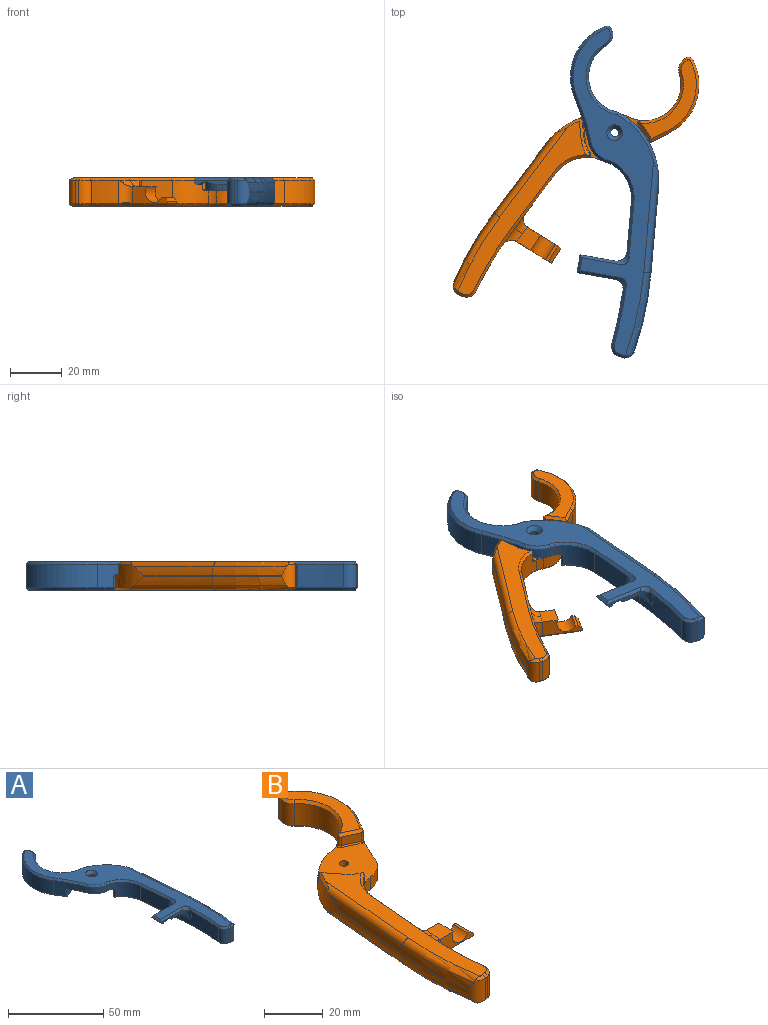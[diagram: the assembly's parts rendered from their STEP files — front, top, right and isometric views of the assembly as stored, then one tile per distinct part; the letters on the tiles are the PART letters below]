
ASSEMBLY  parts=2 mates=1
PART A: 92 faces, bbox 47.6x127.5x23.3 mm
  f0: plane 80.94x16.23mm, normal (0,0,-1), area 509mm2, adj f31,f32,f33,f34,f35,f36,f37,f38
  f1: cylinder r=30mm len=25.84mm, axis (0,0,-1), area 192mm2, adj f2,f11,f14,f31,f47,f66,f68,f69
  f2: cylinder r=14mm len=24.68mm, axis (0,0,-1), area 274.9mm2, adj f1,f14,f18,f45,f57,f81,f89
  f3: plane 9x0.51mm, normal (0.91,0.42,0), area 5.1mm2, adj f18,f26,f41,f60
  f4: cylinder r=21mm len=29.26mm, axis (0,0,-1), area 301.5mm2, adj f19,f26,f42,f63
  f5: cylinder r=10mm len=8.33mm, axis (0,0,-1), area 43.8mm2, adj f14,f19,f46,f91
  f6: plane 26.84x9mm, normal (-1,-0.09,0), area 200.4mm2, adj f7,f27,f37,f49,f75,f77
  f7: cylinder r=150mm len=28.8mm, axis (0,0,-1), area 214.7mm2, adj f6,f29,f39,f56,f76,f78
  f8: plane 9x1.29mm, normal (-0.18,-0.98,0), area 11.8mm2, adj f29,f30,f36,f53
  f9: cylinder r=130mm len=30.93mm, axis (0,0,-1), area 7.1mm2, adj f11,f30,f65,f67
  f10: cylinder r=1.57mm len=3.5mm, axis (0,0,-1), area 34.6mm2, adj f14,f64
  f11: plane 33.28x2.91mm, normal (1,0.09,0), area 7.7mm2, adj f1,f9,f66,f68
  f12: plane 125.47x42.7mm, normal (0,0,1), area 1111.8mm2, adj f40,f41,f42,f43,f44,f45,f46,f47
  f13: plane 33.8x13.25mm, normal (0,0,-1), area 182.3mm2, adj f57,f58,f59,f60,f61,f62,f63
  f14: plane 27.98x22.36mm, normal (0,0,-1), area 362.7mm2, adj f1,f2,f5,f10,f19,f27,f83,f84
  f15: plane 6.71x4.5mm, normal (0.42,-0.91,0), area 33.3mm2, adj f59,f80,f81,f88
  f16: cylinder r=11mm len=4.5mm, axis (0,0,1), area 24.9mm2, adj f17,f33,f79,f85
  f17: plane 5.87x4.59mm, normal (-0.79,0.62,0), area 33.5mm2, adj f16,f32,f82,f84
  f18: cylinder r=5mm len=9mm, axis (0,0,-1), area 58.7mm2, adj f2,f3,f43,f58
  f19: cylinder r=100mm len=16.45mm, axis (0,0,1), area 107.6mm2, adj f4,f5,f14,f44,f61,f80,f87
  f20: plane 14.83x1.7mm, normal (0,-1,0), area 19.4mm2, adj f21,f22,f23,f24,f28,f54,f76,f78
  f21: plane 7x0.2mm, normal (-1,0,0), area 1.4mm2, adj f20,f25,f28,f52
  f22: plane 7x0.64mm, normal (0,0,-1), area 4.5mm2, adj f20,f23,f25,f28
  f23: cylinder r=4mm len=7mm, axis (0,-1,0), area 44.5mm2, adj f20,f22,f24,f25
  f24: plane 7.02x6.78mm, normal (0,0,-1), area 45.6mm2, adj f20,f23,f25,f75,f77,f78
  f25: plane 13.72x1.7mm, normal (0,1,0), area 17.5mm2, adj f21,f22,f23,f24,f28,f50,f75
  f26: cylinder r=2mm len=9mm, axis (0,0,-1), area 30.2mm2, adj f3,f4,f40,f62
  f27: cylinder r=15mm len=12.38mm, axis (0,0,-1), area 132.3mm2, adj f6,f14,f35,f48,f79,f86,f91
  f28: plane 7x1.5mm, normal (-0.71,0,-0.71), area 14.8mm2, adj f20,f21,f22,f25
  f29: cylinder r=4mm len=9mm, axis (0,0,-1), area 53.7mm2, adj f7,f8,f38,f55
  f30: cylinder r=4mm len=9mm, axis (0,0,-1), area 47.1mm2, adj f8,f9,f34,f51,f65,f67,f70,f72
  f31: cone r=29mm half-angle=45deg, axis (0,0,1), area 12.5mm2, adj f0,f1,f32,f71,f82
  f32: plane 7.06x5.58mm, normal (-0.56,0.44,-0.71), area 11.2mm2, adj f0,f17,f31,f33,f82
  f33: cone r=12mm half-angle=45deg, axis (0,0,-1), area 8.8mm2, adj f0,f16,f32,f35,f79
  f34: cone r=3mm half-angle=45deg, axis (0,0,1), area 4.2mm2, adj f0,f30,f36,f72
  f35: cone r=16mm half-angle=45deg, axis (0,0,-1), area 20.6mm2, adj f0,f27,f33,f37,f79
  f36: plane 1.48x1.22mm, normal (-0.13,-0.7,-0.71), area 1.9mm2, adj f0,f8,f34,f38
  f37: plane 26.92x3.34mm, normal (-0.7,-0.06,-0.71), area 38.1mm2, adj f0,f6,f35,f39
  f38: cone r=3mm half-angle=45deg, axis (0,0,1), area 7.4mm2, adj f0,f29,f36,f39
  f39: cone r=150mm half-angle=45deg, axis (0,0,-1), area 40.9mm2, adj f0,f7,f37,f38
  f40: cone r=1mm half-angle=45deg, axis (0,0,-1), area 3.6mm2, adj f12,f26,f41,f42
  f41: plane 1.14x1mm, normal (0.64,0.3,0.71), area 0.8mm2, adj f3,f12,f40,f43
  f42: cone r=21mm half-angle=45deg, axis (0,0,-1), area 46.3mm2, adj f4,f12,f40,f44
  f43: cone r=4mm half-angle=45deg, axis (0,0,-1), area 8.3mm2, adj f12,f18,f41,f45
  f44: cone r=101mm half-angle=45deg, axis (0,0,1), area 26.3mm2, adj f12,f19,f42,f46
  f45: cone r=15mm half-angle=45deg, axis (0,0,1), area 49.9mm2, adj f2,f12,f43,f47
  f46: cone r=10mm half-angle=45deg, axis (0,0,-1), area 15.1mm2, adj f5,f12,f44,f90,f91
  f47: cone r=30mm half-angle=45deg, axis (0,0,-1), area 37.8mm2, adj f1,f12,f45,f69
  f48: cone r=16mm half-angle=45deg, axis (0,0,1), area 25mm2, adj f12,f27,f49,f90,f91
  f49: plane 21.93x2.99mm, normal (-0.7,-0.06,0.71), area 30.3mm2, adj f6,f12,f48,f73,f75
  f50: plane 16.17x1.23mm, normal (0,0.71,0.71), area 21.4mm2, adj f12,f25,f52,f73,f75
  f51: cone r=3mm half-angle=45deg, axis (0,0,-1), area 4.2mm2, adj f12,f30,f53,f70
  f52: plane 7x1mm, normal (-0.71,0,0.71), area 8.5mm2, adj f12,f21,f50,f54
  f53: plane 1.48x1.22mm, normal (-0.13,-0.7,0.71), area 1.9mm2, adj f8,f12,f51,f55
  f54: plane 16.97x1.19mm, normal (0,-0.71,0.71), area 22.6mm2, adj f12,f20,f52,f74,f76
  f55: cone r=3mm half-angle=45deg, axis (0,0,-1), area 7.4mm2, adj f12,f29,f53,f56
  f56: cone r=151mm half-angle=45deg, axis (0,0,1), area 32.2mm2, adj f7,f12,f55,f74,f76
  f57: cone r=14mm half-angle=45deg, axis (0,0,-1), area 41.1mm2, adj f2,f13,f58,f59,f81
  f58: cone r=4mm half-angle=45deg, axis (0,0,1), area 8.3mm2, adj f13,f18,f57,f60
  f59: plane 8.29x4.39mm, normal (0.3,-0.64,-0.71), area 11.8mm2, adj f13,f15,f57,f61,f80,f81
  f60: plane 1.14x1mm, normal (0.64,0.3,-0.71), area 0.8mm2, adj f3,f13,f58,f62
  f61: cone r=101mm half-angle=45deg, axis (0,0,-1), area 9.9mm2, adj f13,f19,f59,f63,f80
  f62: cone r=1mm half-angle=45deg, axis (0,0,1), area 3.6mm2, adj f13,f26,f60,f63
  f63: cone r=20mm half-angle=45deg, axis (0,0,1), area 46.3mm2, adj f4,f13,f61,f62
  f64: cone r=1.57mm half-angle=45deg, axis (0,0,1), area 31mm2, adj f10,f12
  f65: torus R=115mm, axis (0,0,-1), area 111.4mm2, adj f9,f30,f66,f72
  f66: cylinder r=15mm len=38.21mm, axis (0.09,-1,0), area 125.3mm2, adj f1,f11,f65,f71
  f67: torus R=115mm, axis (0,0,1), area 111.4mm2, adj f9,f30,f68,f70
  f68: cylinder r=15mm len=38.21mm, axis (-0.09,1,0), area 125.3mm2, adj f1,f11,f67,f69
  f69: cylinder r=2.5mm len=43.62mm, axis (-0.09,1,0), area 137.8mm2, adj f1,f12,f47,f68,f70
  f70: torus R=127.16mm, axis (0,0,1), area 110.5mm2, adj f12,f30,f51,f67,f69
  f71: cylinder r=2.5mm len=43.62mm, axis (0.09,-1,0), area 137.8mm2, adj f0,f1,f31,f66,f72
  f72: torus R=127.16mm, axis (0,0,1), area 110.5mm2, adj f0,f30,f34,f65,f71
  f73: cylinder r=4mm len=4.23mm, axis (-0.61,0.56,-0.56), area 9.1mm2, adj f12,f49,f50,f75
  f74: bspline ~16.93x16.54mm, area 7.9mm2, adj f12,f54,f56,f76
  f75: cylinder r=4mm len=5.7mm, axis (0,0,1), area 18.6mm2, adj f6,f24,f25,f49,f50,f73,f77
  f76: cylinder r=4mm len=5.7mm, axis (0,0,-1), area 19mm2, adj f7,f20,f54,f56,f74,f78
  f77: cylinder r=4mm len=7.7mm, axis (-0.09,1,0), area 33.8mm2, adj f6,f24,f75,f78
  f78: torus R=146mm, axis (0,0,-1), area 32.9mm2, adj f7,f20,f24,f76,f77
  f79: cylinder r=1mm len=5.06mm, axis (0,0,1), area 10.3mm2, adj f16,f27,f33,f35,f86
  f80: cylinder r=1mm len=4.77mm, axis (0,0,1), area 7mm2, adj f15,f19,f59,f61,f87
  f81: cylinder r=1mm len=5.08mm, axis (0,0,-1), area 10.7mm2, adj f2,f15,f57,f59,f89
  f82: cylinder r=1mm len=4.89mm, axis (0,0,-1), area 8.7mm2, adj f1,f17,f31,f32,f83
  f83: torus R=1.5mm, axis (0,0,1), area 1.3mm2, adj f1,f14,f82,f84
  f84: cylinder r=0.5mm len=6.18mm, axis (-0.62,-0.79,0), area 5.9mm2, adj f14,f17,f83,f85
  f85: torus R=10.5mm, axis (0,0,1), area 4.3mm2, adj f14,f16,f84,f86
  f86: torus R=1.5mm, axis (0,0,1), area 1.6mm2, adj f14,f27,f79,f85
  f87: torus R=1.5mm, axis (0,0,1), area 1mm2, adj f14,f19,f80,f88
  f88: cylinder r=0.5mm len=6.92mm, axis (0.91,0.42,0), area 5.8mm2, adj f14,f15,f87,f89
  f89: torus R=1.5mm, axis (0,0,1), area 1.7mm2, adj f2,f14,f81,f88
  f90: bspline ~2.78x2.43mm, area 2.8mm2, adj f12,f46,f48,f91
  f91: cylinder r=10mm len=4mm, axis (0,0,-1), area 13mm2, adj f5,f14,f27,f46,f48,f90
PART B: 91 faces, bbox 47.6x127.5x23.3 mm
  f0: cylinder r=150mm len=20.94mm, axis (0,0,-1), area 188.7mm2, adj f30,f39,f56,f73
  f1: plane 20.03x9mm, normal (1,-0.09,0), area 181mm2, adj f27,f37,f49,f77
  f2: cylinder r=30mm len=25.84mm, axis (0,0,-1), area 210.7mm2, adj f6,f8,f17,f31,f47,f65,f67,f68
  f3: cylinder r=10mm len=8.33mm, axis (0,0,-1), area 54.7mm2, adj f17,f19,f46,f89
  f4: cylinder r=21mm len=29.26mm, axis (0,0,-1), area 301.5mm2, adj f19,f26,f42,f63
  f5: cylinder r=1.57mm len=6mm, axis (0,0,-1), area 59.4mm2, adj f13,f17
  f6: cylinder r=14mm len=24.68mm, axis (0,0,-1), area 281.4mm2, adj f2,f17,f18,f45,f57,f80,f86
  f7: plane 33.8x13.25mm, normal (0,0,1), area 182.3mm2, adj f57,f58,f59,f60,f61,f62,f63
  f8: plane 33.28x2.91mm, normal (-1,0.09,0), area 7.7mm2, adj f2,f9,f65,f67
  f9: cylinder r=130mm len=30.93mm, axis (0,0,-1), area 7.1mm2, adj f8,f29,f64,f66
  f10: plane 9x1.29mm, normal (0.18,-0.98,0), area 11.8mm2, adj f29,f30,f36,f53
  f11: plane 9x0.51mm, normal (-0.91,0.42,0), area 5.1mm2, adj f18,f26,f41,f60
  f12: plane 80.94x16.23mm, normal (0,0,1), area 509mm2, adj f31,f32,f33,f34,f35,f36,f37,f38
  f13: plane 125.47x42.7mm, normal (0,0,-1), area 1138.7mm2, adj f5,f40,f41,f42,f43,f44,f45,f46
  f14: plane 6.71x3.5mm, normal (-0.42,-0.91,0), area 25.9mm2, adj f59,f79,f80,f87
  f15: plane 5.87x4.59mm, normal (0.79,0.62,0), area 26.1mm2, adj f16,f32,f81,f84
  f16: cylinder r=11mm len=4.33mm, axis (0,0,1), area 19.3mm2, adj f15,f33,f78,f83
  f17: plane 27.98x22.36mm, normal (0,0,1), area 362.7mm2, adj f2,f3,f5,f6,f19,f27,f82,f83
  f18: cylinder r=5mm len=9mm, axis (0,0,-1), area 58.7mm2, adj f6,f11,f43,f58
  f19: cylinder r=100mm len=16.45mm, axis (0,0,1), area 119.5mm2, adj f3,f4,f17,f44,f61,f79,f88
  f20: plane 15.26x6.5mm, normal (0,1,0), area 49mm2, adj f21,f22,f23,f24,f28,f50,f77
  f21: plane 7x6.46mm, normal (0,0,1), area 43.4mm2, adj f20,f24,f25,f73,f74,f75,f77
  f22: plane 7x1mm, normal (1,0,0), area 7mm2, adj f20,f25,f28,f52
  f23: plane 7x1.04mm, normal (0,0,1), area 7.3mm2, adj f20,f24,f25,f28
  f24: cylinder r=4mm len=7.46mm, axis (0,-1,0), area 88mm2, adj f20,f21,f23,f25
  f25: plane 15.83x6.5mm, normal (0,-1,0), area 52.6mm2, adj f21,f22,f23,f24,f28,f54,f73
  f26: cylinder r=2mm len=9mm, axis (0,0,-1), area 30.2mm2, adj f4,f11,f40,f62
  f27: cylinder r=15mm len=12.38mm, axis (0,0,-1), area 134.5mm2, adj f1,f17,f35,f48,f78,f82,f89
  f28: plane 7x1.5mm, normal (0.71,0,0.71), area 14.8mm2, adj f20,f22,f23,f25
  f29: cylinder r=4mm len=9mm, axis (0,0,-1), area 47.1mm2, adj f9,f10,f34,f51,f64,f66,f69,f71
  f30: cylinder r=4mm len=9mm, axis (0,0,-1), area 53.7mm2, adj f0,f10,f38,f55
  f31: cone r=29mm half-angle=45deg, axis (0,0,-1), area 12.5mm2, adj f2,f12,f32,f70,f81
  f32: plane 7.06x5.58mm, normal (0.56,0.44,0.71), area 11.2mm2, adj f12,f15,f31,f33,f81
  f33: cone r=11mm half-angle=45deg, axis (0,0,1), area 8.8mm2, adj f12,f16,f32,f35,f78
  f34: cone r=3mm half-angle=45deg, axis (0,0,-1), area 4.2mm2, adj f12,f29,f36,f71
  f35: cone r=16mm half-angle=45deg, axis (0,0,1), area 20.6mm2, adj f12,f27,f33,f37,f78
  f36: plane 1.48x1.22mm, normal (0.13,-0.7,0.71), area 1.9mm2, adj f10,f12,f34,f38
  f37: plane 26.92x3.34mm, normal (0.7,-0.06,0.71), area 38.1mm2, adj f1,f12,f35,f39,f74
  f38: cone r=3mm half-angle=45deg, axis (0,0,-1), area 7.4mm2, adj f12,f30,f36,f39
  f39: cone r=150mm half-angle=45deg, axis (0,0,1), area 40.9mm2, adj f0,f12,f37,f38,f75
  f40: cone r=1mm half-angle=45deg, axis (0,0,1), area 3.6mm2, adj f13,f26,f41,f42
  f41: plane 1.14x1mm, normal (-0.64,0.3,-0.71), area 0.8mm2, adj f11,f13,f40,f43
  f42: cone r=21mm half-angle=45deg, axis (0,0,1), area 46.3mm2, adj f4,f13,f40,f44
  f43: cone r=4mm half-angle=45deg, axis (0,0,1), area 8.3mm2, adj f13,f18,f41,f45
  f44: cone r=101mm half-angle=45deg, axis (0,0,-1), area 26.3mm2, adj f13,f19,f42,f46
  f45: cone r=15mm half-angle=45deg, axis (0,0,-1), area 49.9mm2, adj f6,f13,f43,f47
  f46: cone r=10mm half-angle=45deg, axis (0,0,1), area 15.1mm2, adj f3,f13,f44,f89,f90
  f47: cone r=30mm half-angle=45deg, axis (0,0,1), area 37.8mm2, adj f2,f13,f45,f68
  f48: cone r=16mm half-angle=45deg, axis (0,0,-1), area 25mm2, adj f13,f27,f49,f89,f90
  f49: plane 21.88x2.94mm, normal (0.7,-0.06,-0.71), area 30.3mm2, adj f1,f13,f48,f76,f77
  f50: plane 17.12x1.1mm, normal (0,0.71,-0.71), area 22.7mm2, adj f13,f20,f52,f76,f77
  f51: cone r=3mm half-angle=45deg, axis (0,0,1), area 4.2mm2, adj f13,f29,f53,f69
  f52: plane 7x1mm, normal (0.71,0,-0.71), area 8.5mm2, adj f13,f22,f50,f54
  f53: plane 1.48x1.22mm, normal (0.13,-0.7,-0.71), area 1.9mm2, adj f10,f13,f51,f55
  f54: plane 17.97x1.19mm, normal (0,-0.71,-0.71), area 24mm2, adj f13,f25,f52,f72,f73
  f55: cone r=3mm half-angle=45deg, axis (0,0,1), area 7.4mm2, adj f13,f30,f53,f56
  f56: cone r=151mm half-angle=45deg, axis (0,0,-1), area 32.2mm2, adj f0,f13,f55,f72,f73
  f57: cone r=14mm half-angle=45deg, axis (0,0,1), area 41.1mm2, adj f6,f7,f58,f59,f80
  f58: cone r=4mm half-angle=45deg, axis (0,0,-1), area 8.3mm2, adj f7,f18,f57,f60
  f59: plane 8.29x4.39mm, normal (-0.3,-0.64,0.71), area 11.8mm2, adj f7,f14,f57,f61,f79,f80
  f60: plane 1.14x1mm, normal (-0.64,0.3,0.71), area 0.8mm2, adj f7,f11,f58,f62
  f61: cone r=101mm half-angle=45deg, axis (0,0,1), area 9.9mm2, adj f7,f19,f59,f63,f79
  f62: cone r=1mm half-angle=45deg, axis (0,0,-1), area 3.6mm2, adj f7,f26,f60,f63
  f63: cone r=20mm half-angle=45deg, axis (0,0,-1), area 46.3mm2, adj f4,f7,f61,f62
  f64: torus R=115mm, axis (0,0,1), area 111.4mm2, adj f9,f29,f65,f71
  f65: cylinder r=15mm len=38.21mm, axis (0.09,1,0), area 125.3mm2, adj f2,f8,f64,f70
  f66: torus R=115mm, axis (0,0,-1), area 111.4mm2, adj f9,f29,f67,f69
  f67: cylinder r=15mm len=38.21mm, axis (-0.09,-1,0), area 125.3mm2, adj f2,f8,f66,f68
  f68: cylinder r=2.5mm len=43.62mm, axis (-0.09,-1,0), area 137.8mm2, adj f2,f13,f47,f67,f69
  f69: torus R=127.16mm, axis (0,0,1), area 110.5mm2, adj f13,f29,f51,f66,f68
  f70: cylinder r=2.5mm len=43.62mm, axis (0.09,1,0), area 137.8mm2, adj f2,f12,f31,f65,f71
  f71: torus R=127.16mm, axis (0,0,1), area 110.5mm2, adj f12,f29,f34,f64,f70
  f72: bspline ~17.09x16.69mm, area 7.9mm2, adj f13,f54,f56,f73
  f73: cylinder r=4mm len=9mm, axis (0,0,-1), area 45.3mm2, adj f0,f21,f25,f54,f56,f72,f75
  f74: cylinder r=4mm len=7.13mm, axis (0.09,1,0), area 24.1mm2, adj f21,f37,f75,f77
  f75: torus R=146.29mm, axis (0,0,1), area 27.4mm2, adj f21,f39,f73,f74
  f76: cylinder r=4mm len=4.14mm, axis (-0.61,-0.56,-0.56), area 8.3mm2, adj f13,f49,f50,f77
  f77: cylinder r=3.5mm len=9mm, axis (0,0,-1), area 43mm2, adj f1,f20,f21,f49,f50,f74,f76
  f78: cylinder r=1mm len=4.06mm, axis (0,0,-1), area 8.2mm2, adj f16,f27,f33,f35,f82
  f79: cylinder r=1mm len=3.77mm, axis (0,0,1), area 5.5mm2, adj f14,f19,f59,f61,f88
  f80: cylinder r=1mm len=4.08mm, axis (0,0,-1), area 8.5mm2, adj f6,f14,f57,f59,f86
  f81: cylinder r=1mm len=3.89mm, axis (0,0,-1), area 6.9mm2, adj f2,f15,f31,f32,f85
  f82: torus R=1.5mm, axis (0,0,1), area 1.6mm2, adj f17,f27,f78,f83
  f83: torus R=10.5mm, axis (0,0,1), area 4.3mm2, adj f16,f17,f82,f84
  f84: cylinder r=0.5mm len=6.18mm, axis (0.62,-0.79,0), area 5.9mm2, adj f15,f17,f83,f85
  f85: torus R=1.5mm, axis (0,0,1), area 1.3mm2, adj f2,f17,f81,f84
  f86: torus R=1.5mm, axis (0,0,1), area 1.7mm2, adj f6,f17,f80,f87
  f87: cylinder r=0.5mm len=6.92mm, axis (-0.91,0.42,0), area 5.8mm2, adj f14,f17,f86,f88
  f88: torus R=1.5mm, axis (0,0,1), area 1mm2, adj f17,f19,f79,f87
  f89: cylinder r=10mm len=5mm, axis (0,0,-1), area 16.3mm2, adj f3,f17,f27,f46,f48,f90
  f90: bspline ~2.78x2.43mm, area 2.8mm2, adj f13,f46,f48,f89
PLACE A rot(axis=(0,0,-1),10deg) t=(-14.75,51.07,7.85)mm
PLACE B rot(axis=(0,0,-1),32deg) t=(-6.91,48.06,7.85)mm
MATE revolute A.f10 <-> B.f5  axis (0,0,-1) through (-18.57,29.41,13.85)mm
